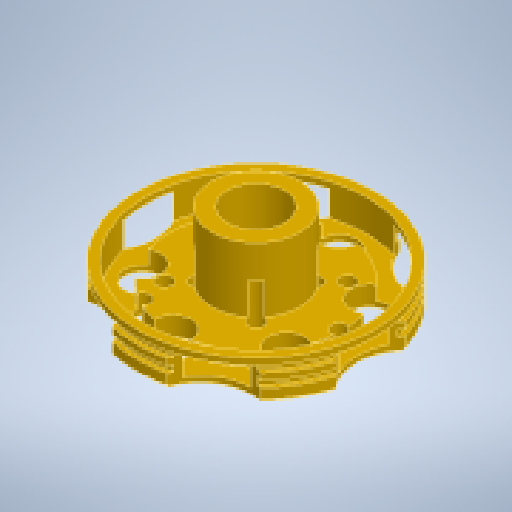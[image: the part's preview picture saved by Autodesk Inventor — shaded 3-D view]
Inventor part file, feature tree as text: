
AUTODESK INVENTOR PART (.ipt)
format: ipt  version: 2023.1 (Build 271208000, 208)  size: 433,152 bytes
history: native  units: in
note: dims shown in document units (in); Inventor stores cm internally (conversion verified against a paired STEP export)
features: sketch x2, chamfer x2, extrude x2, revolve x1
ambient origin geometry x8: Origin, YZ Plane, XZ Plane, XY Plane, X Axis, Y Axis, Z Axis, Center Point
bodies: Solid1 (feature_tree)
feature tree (7):
  revolve  "Revolution1"  [1 undecoded]
  sketch  "Sketch2"  dims[d2=0.0531in d3=0.0689in d4=0.0591in d5=0.0492in d6=0.0492in d7=0.7874in d9=0.0984in d10=0.3937in d12=0.3937in d14=0.6496in d15=0.1575in d16=0.2165in d17=0.6496in d18=0.3346in d19=90.0deg d20=1.2598in d21=0.2756in d22=30.0deg d23=1.5354in d24=0.7874in d25=0.6299in d26=0.748in d27=0.9843in d28=45.0deg d30=0.1181in d31=0.1181in d32=0.1181in d33=0.7874in d35=360.0deg d37=2.3622in d39=360.0deg d41=1.2402in d42=30.0deg d43=0.1181in d44=1.1811in d46=360.0deg d48=0.0197in d49=0.0787in d50=45.0deg d51=0.2461in d52=0.0in d53=0.3937in d54=0.0in d55=0.0098in d56=0.0787in d57=45.0deg d58=0.4626in d59=1.3386in d60=0.1575in]
  chamfer  "Chamfer1"  Distance=0.0689in
  extrude  "Extrusion1"  Depth=0.3937in
  extrude  "Extrusion2"  Depth=0.3937in
  chamfer  "Chamfer2"  Distance=0.0492in
  sketch  "Sketch1"  dims[d0=0.9055in d1=0.2953in]
note: 1 required parameter value undecoded (feature->parameter linkage not recoverable at this tier; creation-order binding heuristic only, values carry confidence <= 0.55)
